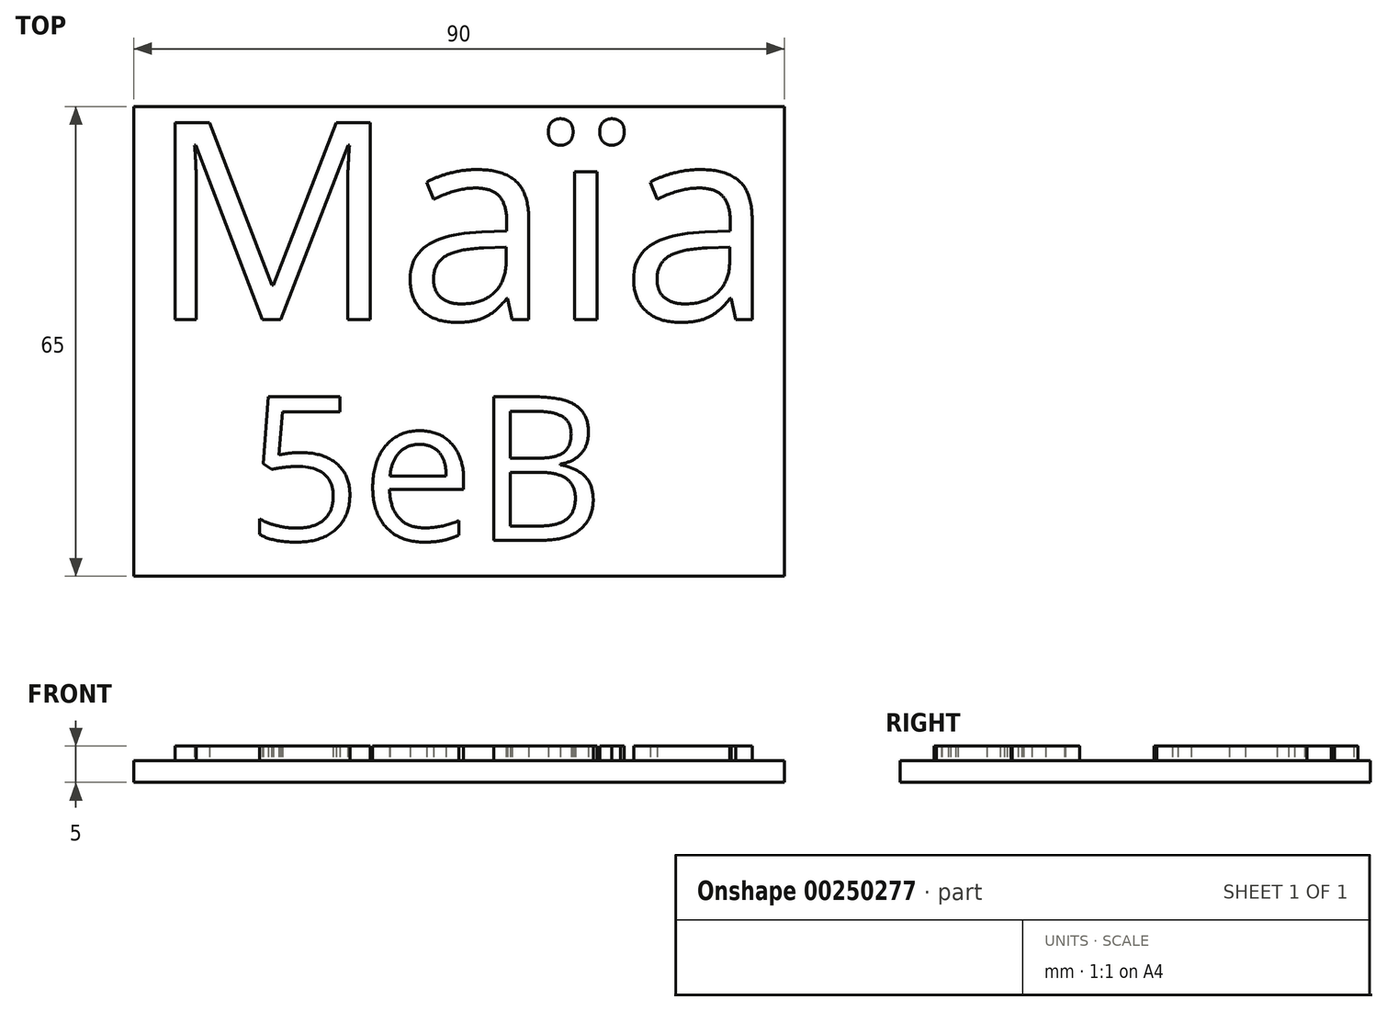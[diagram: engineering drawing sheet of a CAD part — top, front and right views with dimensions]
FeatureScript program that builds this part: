
annotation { "Feature Type Name" : "Feature", "Feature Type Description" : "" }
export const myFeature = defineFeature(function(context is Context, id is Id, definition is map)
    precondition{}
    {
        {
            var Q0;
            Q0=qCreatedBy(makeId("Top.planeOp"),FACE);
            var sketch = newSketch(context, id + "F0", { "sketchPlane" : qUnion([Q0])});
            skLineSegment(sketch, "E0.bottom", {"start": v(0, 0) * mm, "end": v(90, 0) * mm});
            skLineSegment(sketch, "E0.top", {"start": v(0, -65) * mm, "end": v(90, -65) * mm});
            skLineSegment(sketch, "E0.left", {"start": v(0, 0) * mm, "end": v(0, -65) * mm});
            skLineSegment(sketch, "E0.right", {"start": v(90, 0) * mm, "end": v(90, -65) * mm});
            skSolve(sketch);
        }
        {
            var Q0;
            Q0=makeQuery(id+"F0.imprint","IMPRINT",FACE,{"disambiguationData":[TD([[makeQuery(id+"F0.imprint","IMPRINT",EDGE,{"derivedFrom":sQuery(id+"F0.wireOp",EDGE,"E0.bottom")}),-1.0]])]});
            extrude(context, id + "F1", {"entities" : qUnion([Q0]), "depth" : 3 * mm});
        }
        {
            var Q0;
            Q0=makeQuery(id+"F1.opExtrude","CAP_FACE",FACE,{"disambiguationData":[OSD([sQuery(id+"F0.wireOp",EDGE,"E0.bottom"),sQuery(id+"F0.wireOp",EDGE,"E0.top"),sQuery(id+"F0.wireOp",EDGE,"E0.left"),sQuery(id+"F0.wireOp",EDGE,"E0.right")])],"isStart":false});
            var sketch = newSketch(context, id + "F2", { "sketchPlane" : qUnion([Q0])});
            skText(sketch, "E1", { "text": "Maïa", "fontName": "OpenSans-Regular.ttf"});
            skText(sketch, "E2", { "text": "5eB", "fontName": "OpenSans-Regular.ttf"});
            const initialGuessF2  = {"E1": [0.002, -0.0295, 1, 0, 0.0275], "E2": [0.01562, -0.06, 1, 0, 0.02]};
            skSetInitialGuess(sketch, initialGuessF2);
            skSolve(sketch);
        }
        {
            var Q0;
            Q0 = qSketchRegion(id + "F2", true);
            extrude(context, id + "F3", {"entities" : qUnion([Q0]), "operationType" : NewBodyOperationType.ADD, "depth" : 2 * mm});
        }
    });
